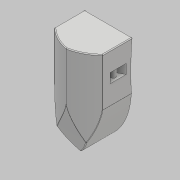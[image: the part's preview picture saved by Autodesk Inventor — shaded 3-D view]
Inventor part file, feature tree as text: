
AUTODESK INVENTOR PART (.ipt)
format: ipt  version: 2018 (Build 220112000, 112)  size: 362,496 bytes
history: native  units: mm
features: extrude x8, sketch x8, projected_geometry x4, plane x2, mirror x2, other x1, fillet x1
ambient origin geometry x8: Origin, YZ Plane, XZ Plane, XY Plane, X Axis, Y Axis, Z Axis, Center Point
bodies: Body1 (feature_tree)
feature tree (26):
  other  "實體1"
  extrude  "擠出1"  Depth=30.0mm
  extrude  "擠出2"  Depth=30.0mm
  plane  "工作平面1"
  mirror  "鏡射1"
  extrude  "擠出3"  Depth=30.0mm TaperAngle=0.0deg
  mirror  "鏡射2"
  extrude  "擠出4"  Depth=66.75mm TaperAngle=0.0deg
  extrude  "擠出5"  Depth=66.75mm TaperAngle=0.0deg
  extrude  "擠出6"  Depth=5.0mm
  fillet  "圓角1"  Radius=21.75mm
  plane  "工作平面2"
  extrude  "擠出7"  Depth=378.75mm TaperAngle=0.0deg
  extrude  "擠出8"  Depth=154.5mm TaperAngle=0.0deg
  sketch  "草圖1"
  sketch  "草圖2"
  projected_geometry  "投影迴路1"
  sketch  "草圖3"
  projected_geometry  "投影迴路2"
  sketch  "草圖4"
  projected_geometry  "投影迴路3"
  sketch  "草圖5"
  sketch  "草圖6"
  sketch  "草圖7"
  sketch  "草圖8"
  projected_geometry  "投影迴路4"
